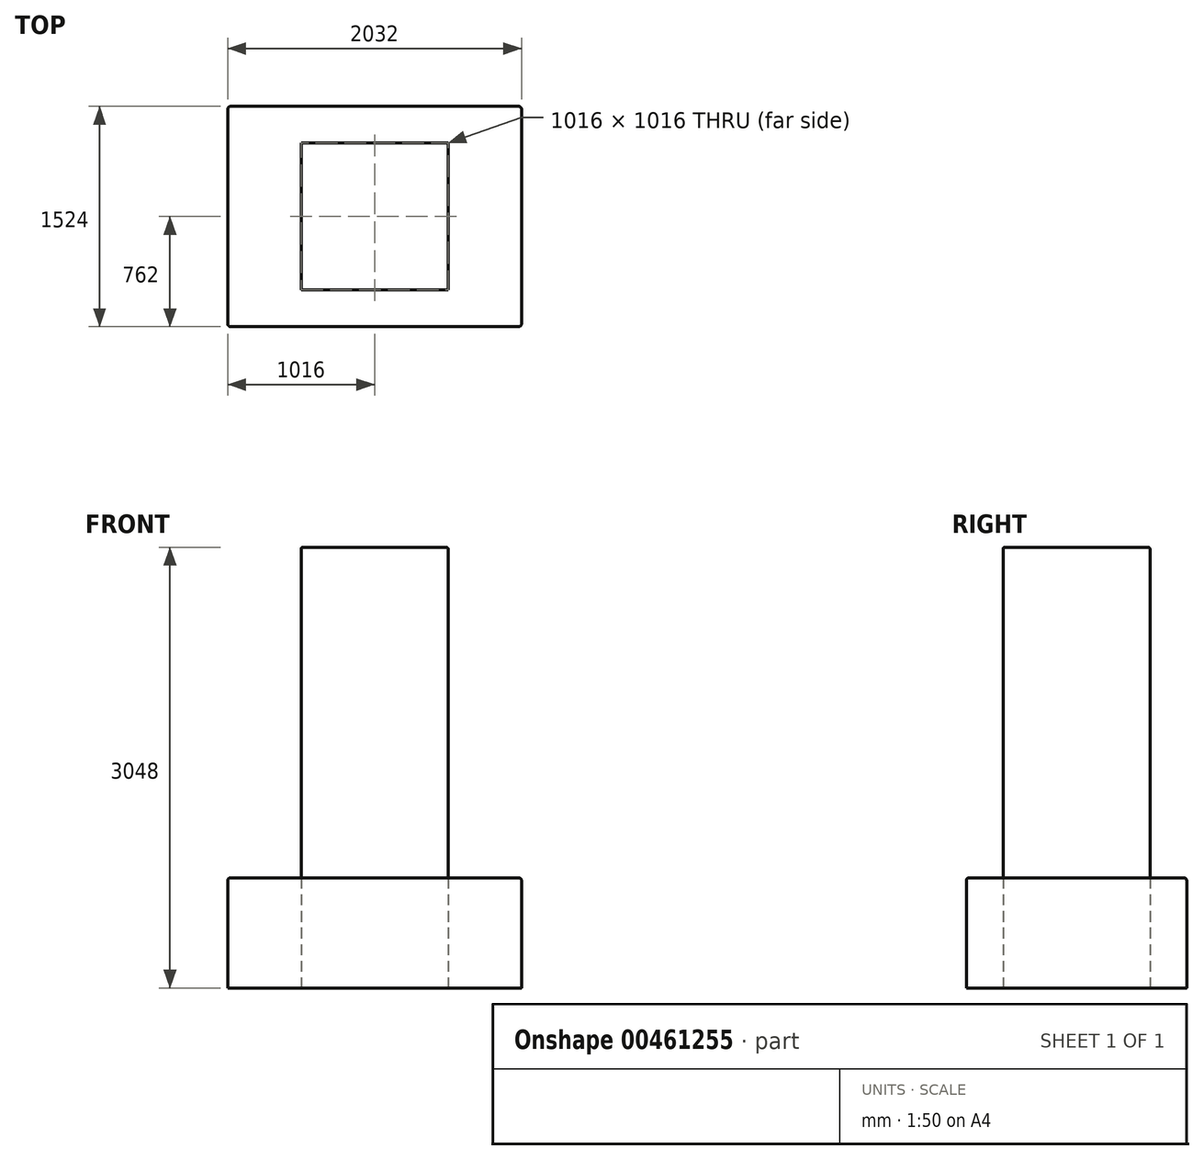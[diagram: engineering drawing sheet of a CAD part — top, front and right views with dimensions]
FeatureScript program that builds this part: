
annotation { "Feature Type Name" : "Feature", "Feature Type Description" : "" }
export const myFeature = defineFeature(function(context is Context, id is Id, definition is map)
    precondition{}
    {
        {
            var Q0;
            Q0=qCreatedBy(makeId("Top.planeOp"),FACE);
            var sketch = newSketch(context, id + "F0", { "sketchPlane" : qUnion([Q0])});
            skLineSegment(sketch, "E0.bottom", {"start": v(508, 508) * mm, "end": v(-508, 508) * mm});
            skLineSegment(sketch, "E0.top", {"start": v(508, -508) * mm, "end": v(-508, -508) * mm});
            skLineSegment(sketch, "E0.left", {"start": v(508, 508) * mm, "end": v(508, -508) * mm});
            skLineSegment(sketch, "E0.right", {"start": v(-508, 508) * mm, "end": v(-508, -508) * mm});
            skPoint(sketch, "E0.middle", {"position": v(0, 0) * mm});
            skSolve(sketch);
        }
        {
            var Q0;
            Q0=makeQuery(id+"F0.imprint","IMPRINT",FACE,{"disambiguationData":[TD([[makeQuery(id+"F0.imprint","IMPRINT",EDGE,{"derivedFrom":sQuery(id+"F0.wireOp",EDGE,"E0.bottom")}),1.0]])]});
            extrude(context, id + "F1", {"entities" : qUnion([Q0]), "depth" : 3048 * mm});
        }
        {
            var Q0;
            Q0=makeQuery(id+"F0.imprint","IMPRINT",FACE,{"disambiguationData":[TD([[makeQuery(id+"F0.imprint","IMPRINT",EDGE,{"derivedFrom":sQuery(id+"F0.wireOp",EDGE,"E0.bottom")}),1.0]])]});
            var sketch = newSketch(context, id + "F2", { "sketchPlane" : qUnion([Q0])});
            skLineSegment(sketch, "E1", {"start": v(0, 0) * mm, "end": v(1016, 0) * mm});
            skLineSegment(sketch, "E2", {"start": v(1016, 0) * mm, "end": v(0, 0) * mm});
            skLineSegment(sketch, "E3", {"start": v(0, 0) * mm, "end": v(-1016, 0) * mm});
            skLineSegment(sketch, "E4", {"start": v(0, 0) * mm, "end": v(0, -762) * mm});
            skLineSegment(sketch, "E5", {"start": v(0, 0) * mm, "end": v(0, 762) * mm});
            skLineSegment(sketch, "E6.bottom", {"start": v(-1016, 0) * mm, "end": v(0, 0) * mm});
            skLineSegment(sketch, "E6.top", {"start": v(-1016, -762) * mm, "end": v(0, -762) * mm});
            skLineSegment(sketch, "E6.left", {"start": v(-1016, 0) * mm, "end": v(-1016, -762) * mm});
            skLineSegment(sketch, "E7.left", {"start": v(0, 0) * mm, "end": v(0, 0) * mm});
            skLineSegment(sketch, "E7.right", {"start": v(1016, 0) * mm, "end": v(1016, 0) * mm});
            skLineSegment(sketch, "E8.bottom", {"start": v(0, -762) * mm, "end": v(1016, -762) * mm});
            skLineSegment(sketch, "E8.left", {"start": v(0, -762) * mm, "end": v(0, 0) * mm});
            skLineSegment(sketch, "E8.right", {"start": v(1016, -762) * mm, "end": v(1016, 0) * mm});
            skLineSegment(sketch, "E9.bottom", {"start": v(0, 762) * mm, "end": v(1016, 762) * mm});
            skLineSegment(sketch, "E9.left", {"start": v(0, 762) * mm, "end": v(0, 0) * mm});
            skLineSegment(sketch, "E9.right", {"start": v(1016, 762) * mm, "end": v(1016, 0) * mm});
            skLineSegment(sketch, "E10.bottom", {"start": v(0, 762) * mm, "end": v(-1016, 762) * mm});
            skLineSegment(sketch, "E10.right", {"start": v(-1016, 762) * mm, "end": v(-1016, 0) * mm});
            skSolve(sketch);
        }
        {
            var Q0;
            {var subQ1=sQuery(id+"F2.wireOp",EDGE,"E10.bottom");Q0=makeQuery(id+"F2.imprint","IMPRINT",FACE,{"disambiguationData":[TD([[makeQuery(id+"F2.imprint","IMPRINT",EDGE,{"derivedFrom":subQ1}),1.0]])]});}
            var Q1;
            {var subQ7=sQuery(id+"F2.wireOp",EDGE,"E9.bottom");Q1=makeQuery(id+"F2.imprint","IMPRINT",FACE,{"disambiguationData":[TD([[makeQuery(id+"F2.imprint","IMPRINT",EDGE,{"derivedFrom":subQ7}),-1.0]])]});}
            var Q2;
            {var subQ5=sQuery(id+"F2.wireOp",EDGE,"E8.bottom");Q2=makeQuery(id+"F2.imprint","IMPRINT",FACE,{"disambiguationData":[TD([[makeQuery(id+"F2.imprint","IMPRINT",EDGE,{"derivedFrom":subQ5}),1.0]])]});}
            var Q3;
            {var subQ7=sQuery(id+"F2.wireOp",EDGE,"E6.top");Q3=makeQuery(id+"F2.imprint","IMPRINT",FACE,{"disambiguationData":[TD([[makeQuery(id+"F2.imprint","IMPRINT",EDGE,{"derivedFrom":subQ7}),1.0]])]});}
            extrude(context, id + "F3", {"entities" : qUnion([Q0, Q1, Q2, Q3]), "depth" : 762 * mm});
        }
        {
            var Q0;
            Q0=makeQuery(id+"F3.opExtrude","SWEPT_EDGE",EDGE,{"disambiguationData":[OSD([sQuery(id+"F2.wireOp",EDGE,"E9.bottom"),sQuery(id+"F2.wireOp",EDGE,"E9.right")])]});
            var Q1;
            Q1=makeQuery(id+"F3.opExtrude","CAP_EDGE",EDGE,{"disambiguationData":[OSD([sQuery(id+"F2.wireOp",EDGE,"E9.bottom"),sQuery(id+"F2.wireOp",EDGE,"E10.bottom")])],"isStart":false});
            var Q2;
            Q2=makeQuery(id+"F3.opExtrude","SWEPT_EDGE",EDGE,{"disambiguationData":[OSD([sQuery(id+"F2.wireOp",EDGE,"E10.bottom"),sQuery(id+"F2.wireOp",EDGE,"E10.right")])]});
            var Q3;
            Q3=makeQuery(id+"F3.opExtrude","CAP_EDGE",EDGE,{"disambiguationData":[OSD([sQuery(id+"F2.wireOp",EDGE,"E8.right"),sQuery(id+"F2.wireOp",EDGE,"E9.right")])],"isStart":false});
            var Q4;
            Q4=makeQuery(id+"F3.opExtrude","SWEPT_EDGE",EDGE,{"disambiguationData":[OSD([sQuery(id+"F2.wireOp",EDGE,"E8.bottom"),sQuery(id+"F2.wireOp",EDGE,"E8.right")])]});
            var Q5;
            Q5=makeQuery(id+"F3.opExtrude","CAP_EDGE",EDGE,{"disambiguationData":[OSD([sQuery(id+"F2.wireOp",EDGE,"E6.top"),sQuery(id+"F2.wireOp",EDGE,"E8.bottom")])],"isStart":false});
            var Q6;
            Q6=makeQuery(id+"F3.opExtrude","SWEPT_EDGE",EDGE,{"disambiguationData":[OSD([sQuery(id+"F2.wireOp",EDGE,"E6.top"),sQuery(id+"F2.wireOp",EDGE,"E6.left")])]});
            var Q7;
            Q7=makeQuery(id+"F3.opExtrude","CAP_EDGE",EDGE,{"disambiguationData":[OSD([sQuery(id+"F2.wireOp",EDGE,"E6.left"),sQuery(id+"F2.wireOp",EDGE,"E10.right")])],"isStart":false});
            fillet(context, id + "F4", {"entities" : qUnion([Q0, Q1, Q2, Q3, Q4, Q5, Q6, Q7]), "radius" : 20.32 * mm, "tangentPropagation" : true, "allowEdgeOverflow" : false});
        }
        {
            var Q0;
            Q0=makeQuery(id+"F1.opExtrude","SWEPT_EDGE",EDGE,{"disambiguationData":[OSD([sQuery(id+"F0.wireOp",EDGE,"E0.bottom"),sQuery(id+"F0.wireOp",EDGE,"E0.left")])]});
            var Q1;
            Q1=makeQuery(id+"F1.opExtrude","SWEPT_EDGE",EDGE,{"disambiguationData":[OSD([sQuery(id+"F0.wireOp",EDGE,"E0.bottom"),sQuery(id+"F0.wireOp",EDGE,"E0.right")])]});
            var Q2;
            Q2=makeQuery(id+"F1.opExtrude","SWEPT_EDGE",EDGE,{"disambiguationData":[OSD([sQuery(id+"F0.wireOp",EDGE,"E0.top"),sQuery(id+"F0.wireOp",EDGE,"E0.right")])]});
            var Q3;
            Q3=makeQuery(id+"F1.opExtrude","SWEPT_EDGE",EDGE,{"disambiguationData":[OSD([sQuery(id+"F0.wireOp",EDGE,"E0.top"),sQuery(id+"F0.wireOp",EDGE,"E0.left")])]});
            var Q4;
            Q4=makeQuery(id+"F1.opExtrude","CAP_EDGE",EDGE,{"disambiguationData":[OSD([sQuery(id+"F0.wireOp",EDGE,"E0.bottom")])],"isStart":false});
            var Q5;
            Q5=makeQuery(id+"F1.opExtrude","CAP_EDGE",EDGE,{"disambiguationData":[OSD([sQuery(id+"F0.wireOp",EDGE,"E0.right")])],"isStart":false});
            var Q6;
            Q6=makeQuery(id+"F1.opExtrude","CAP_EDGE",EDGE,{"disambiguationData":[OSD([sQuery(id+"F0.wireOp",EDGE,"E0.left")])],"isStart":false});
            var Q7;
            Q7=makeQuery(id+"F1.opExtrude","CAP_EDGE",EDGE,{"disambiguationData":[OSD([sQuery(id+"F0.wireOp",EDGE,"E0.top")])],"isStart":false});
            fillet(context, id + "F5", {"entities" : qUnion([Q0, Q1, Q2, Q3, Q4, Q5, Q6, Q7]), "radius" : 12.7 * mm, "tangentPropagation" : true, "allowEdgeOverflow" : false});
        }
    });
